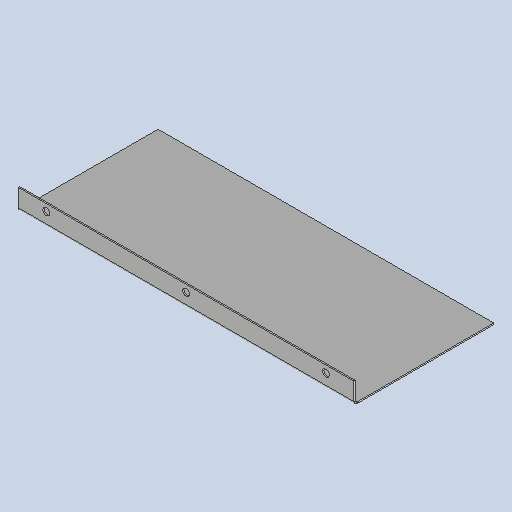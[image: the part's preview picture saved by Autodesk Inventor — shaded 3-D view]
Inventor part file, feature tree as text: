
AUTODESK INVENTOR PART (.ipt)
format: ipt  version: 2025 (Build 290162010, 162A)  size: 373,760 bytes
history: native  units: mm
features: other x6, sheet_metal_op x4, sketch x4, pattern_linear x1, projected_geometry x1
ambient origin geometry x8: Origin, YZ Plane, XZ Plane, XY Plane, X Axis, Y Axis, Z Axis, Center Point
bodies: Solid1 (feature_tree)
feature tree (16):
  sheet_metal_op  "Face1"
  other  "Mark1"
  sheet_metal_op  "Flange1"
  pattern_linear  "Rectangular Pattern1"  Count1=48  [1 undecoded]
  other  "A-Side Definition"
  sketch  "Sketch1"  dims[d1=200.0mm]
  other  "Plate1"
  sketch  "Sketch2"  dims[d2=2.0mm]
  sketch  "Sketch3"  dims[d6=200.0mm]
  other  "Plate2"
  sheet_metal_op  "Bend1"
  sheet_metal_op  "Corner1"
  sketch  "Sketch4"  dims[d9=20.0mm d10=20.0mm d11=20.0mm d12=2.0mm d13=1.0mm d14=4.0mm d15=2.75mm d16=30.0mm d17=90.0deg d18=2.75mm d19=8.0mm d20=2.0mm d21=2.75mm d22=10.0mm d23=10.0mm d24=2.0mm d25=0.0mm d26=30.0mm d28=200.0mm]
  projected_geometry  "Projected Loop1"
  other  "Cut1"
  other  "Definition1"
note: 1 required parameter value undecoded (feature->parameter linkage not recoverable at this tier; creation-order binding heuristic only, values carry confidence <= 0.55)
